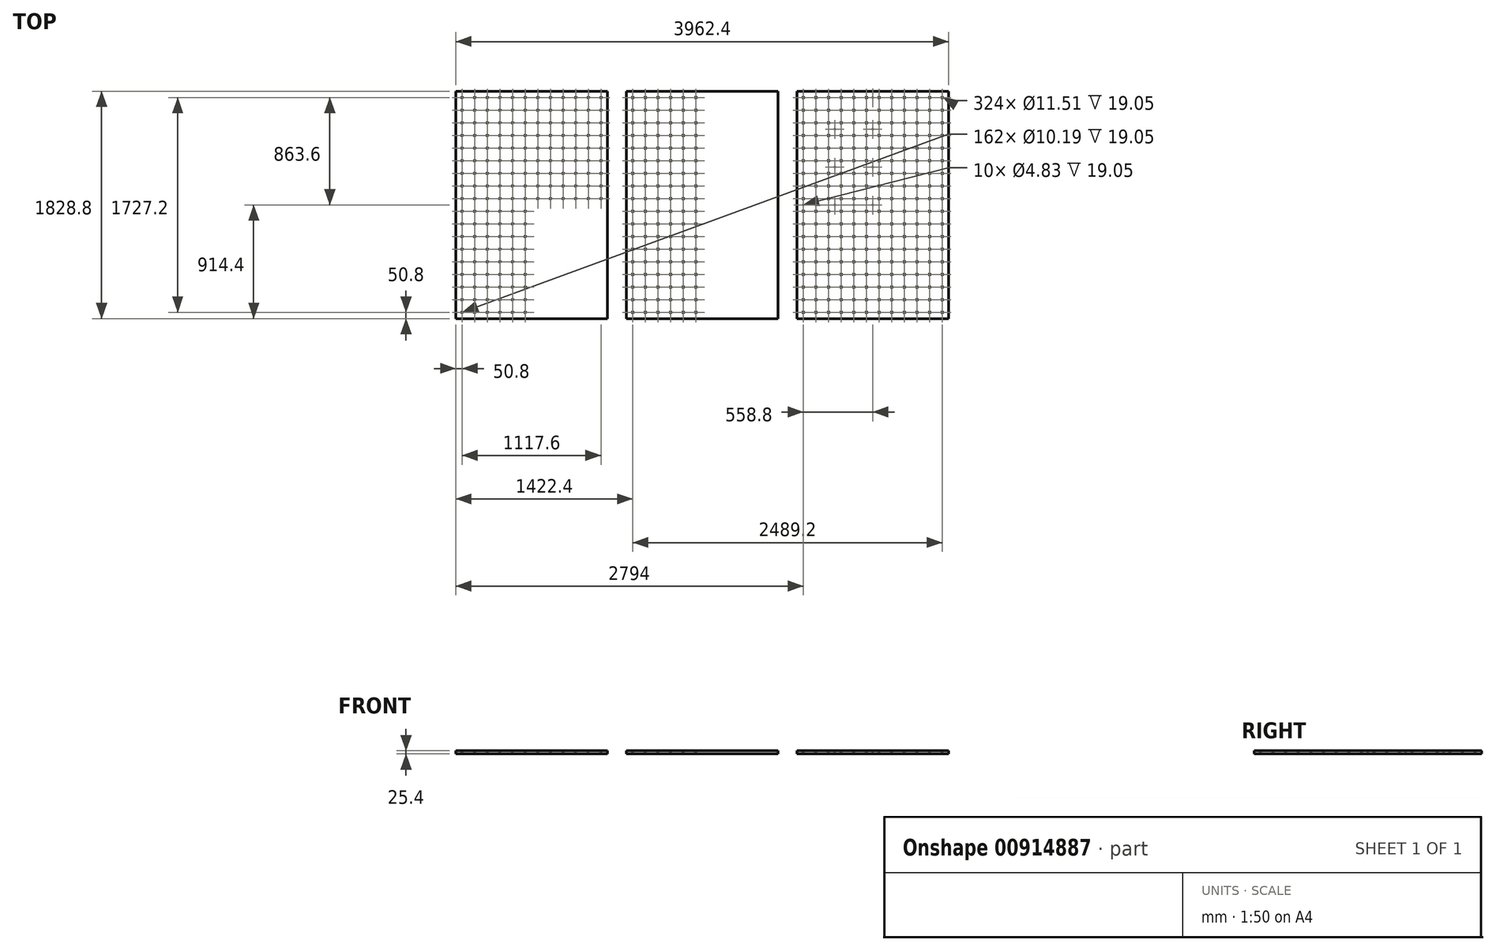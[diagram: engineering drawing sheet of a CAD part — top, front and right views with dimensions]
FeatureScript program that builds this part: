
annotation { "Feature Type Name" : "Feature", "Feature Type Description" : "" }
export const myFeature = defineFeature(function(context is Context, id is Id, definition is map)
    precondition{}
    {
        {
            var Q0;
            Q0=qCreatedBy(makeId("Top.planeOp"),FACE);
            var sketch = newSketch(context, id + "F0", { "sketchPlane" : qUnion([Q0])});
            skLineSegment(sketch, "E0.bottom", {"start": v(0, 1828.8) * mm, "end": v(1219.2, 1828.8) * mm});
            skLineSegment(sketch, "E0.top", {"start": v(0, 0) * mm, "end": v(1219.2, 0) * mm});
            skLineSegment(sketch, "E0.left", {"start": v(0, 1828.8) * mm, "end": v(0, 0) * mm});
            skLineSegment(sketch, "E0.right", {"start": v(1219.2, 1828.8) * mm, "end": v(1219.2, 0) * mm});
            skLineSegment(sketch, "E1", {"start": v(609.6, 1219.2) * mm, "end": v(609.6, 609.6) * mm, "construction": true});
            skLineSegment(sketch, "E2", {"start": v(304.8, 914.4) * mm, "end": v(914.4, 914.4) * mm, "construction": true});
            skSolve(sketch);
        }
        {
            var Q0;
            Q0=makeQuery(id+"F0.imprint","IMPRINT",FACE,{"disambiguationData":[TD([[makeQuery(id+"F0.imprint","IMPRINT",EDGE,{"derivedFrom":sQuery(id+"F0.wireOp",EDGE,"E0.bottom")}),-1.0]])]});
            extrude(context, id + "F1", {"entities" : qUnion([Q0]), "depth" : 25.4 * mm, "offsetDistance" : 25.4 * mm});
        }
        {
            var Q0;
            Q0=makeQuery(id+"F1.opExtrude","CAP_FACE",FACE,{"disambiguationData":[OSD([sQuery(id+"F0.wireOp",EDGE,"E0.bottom"),sQuery(id+"F0.wireOp",EDGE,"E0.top"),sQuery(id+"F0.wireOp",EDGE,"E0.left"),sQuery(id+"F0.wireOp",EDGE,"E0.right")])],"isStart":false});
            var sketch = newSketch(context, id + "F2", { "sketchPlane" : qUnion([Q0])});
            skCircle(sketch, "E3", {"center": v(558.8, 965.2) * mm, "radius": 5.75 * mm});
            skCircle(sketch, "E4.0.1.0", {"center": v(558.8, 1066.8) * mm, "radius": 5.75 * mm});
            skCircle(sketch, "E4.0.2.0", {"center": v(558.8, 1168.4) * mm, "radius": 5.75 * mm});
            skCircle(sketch, "E4.0.3.0", {"center": v(558.8, 1270) * mm, "radius": 5.75 * mm});
            skCircle(sketch, "E4.0.4.0", {"center": v(558.8, 1371.6) * mm, "radius": 5.75 * mm});
            skCircle(sketch, "E4.0.5.0", {"center": v(558.8, 1473.2) * mm, "radius": 5.75 * mm});
            skCircle(sketch, "E4.0.6.0", {"center": v(558.8, 1574.8) * mm, "radius": 5.75 * mm});
            skCircle(sketch, "E4.0.7.0", {"center": v(558.8, 1676.4) * mm, "radius": 5.75 * mm});
            skCircle(sketch, "E4.0.8.0", {"center": v(558.8, 1778) * mm, "radius": 5.75 * mm});
            skCircle(sketch, "E4.1.0.0", {"center": v(457.2, 965.2) * mm, "radius": 5.75 * mm});
            skCircle(sketch, "E4.1.1.0", {"center": v(457.2, 1066.8) * mm, "radius": 5.75 * mm});
            skCircle(sketch, "E4.1.2.0", {"center": v(457.2, 1168.4) * mm, "radius": 5.75 * mm});
            skCircle(sketch, "E4.1.3.0", {"center": v(457.2, 1270) * mm, "radius": 5.75 * mm});
            skCircle(sketch, "E4.1.4.0", {"center": v(457.2, 1371.6) * mm, "radius": 5.75 * mm});
            skCircle(sketch, "E4.1.5.0", {"center": v(457.2, 1473.2) * mm, "radius": 5.75 * mm});
            skCircle(sketch, "E4.1.6.0", {"center": v(457.2, 1574.8) * mm, "radius": 5.75 * mm});
            skCircle(sketch, "E4.1.7.0", {"center": v(457.2, 1676.4) * mm, "radius": 5.75 * mm});
            skCircle(sketch, "E4.1.8.0", {"center": v(457.2, 1778) * mm, "radius": 5.75 * mm});
            skCircle(sketch, "E4.2.0.0", {"center": v(355.6, 965.2) * mm, "radius": 5.75 * mm});
            skCircle(sketch, "E4.2.1.0", {"center": v(355.6, 1066.8) * mm, "radius": 5.75 * mm});
            skCircle(sketch, "E4.2.2.0", {"center": v(355.6, 1168.4) * mm, "radius": 5.75 * mm});
            skCircle(sketch, "E4.2.3.0", {"center": v(355.6, 1270) * mm, "radius": 5.75 * mm});
            skCircle(sketch, "E4.2.4.0", {"center": v(355.6, 1371.6) * mm, "radius": 5.75 * mm});
            skCircle(sketch, "E4.2.5.0", {"center": v(355.6, 1473.2) * mm, "radius": 5.75 * mm});
            skCircle(sketch, "E4.2.6.0", {"center": v(355.6, 1574.8) * mm, "radius": 5.75 * mm});
            skCircle(sketch, "E4.2.7.0", {"center": v(355.6, 1676.4) * mm, "radius": 5.75 * mm});
            skCircle(sketch, "E4.2.8.0", {"center": v(355.6, 1778) * mm, "radius": 5.75 * mm});
            skCircle(sketch, "E4.3.0.0", {"center": v(254, 965.2) * mm, "radius": 5.75 * mm});
            skCircle(sketch, "E4.3.1.0", {"center": v(254, 1066.8) * mm, "radius": 5.75 * mm});
            skCircle(sketch, "E4.3.2.0", {"center": v(254, 1168.4) * mm, "radius": 5.75 * mm});
            skCircle(sketch, "E4.3.3.0", {"center": v(254, 1270) * mm, "radius": 5.75 * mm});
            skCircle(sketch, "E4.3.4.0", {"center": v(254, 1371.6) * mm, "radius": 5.75 * mm});
            skCircle(sketch, "E4.3.5.0", {"center": v(254, 1473.2) * mm, "radius": 5.75 * mm});
            skCircle(sketch, "E4.3.6.0", {"center": v(254, 1574.8) * mm, "radius": 5.75 * mm});
            skCircle(sketch, "E4.3.7.0", {"center": v(254, 1676.4) * mm, "radius": 5.75 * mm});
            skCircle(sketch, "E4.3.8.0", {"center": v(254, 1778) * mm, "radius": 5.75 * mm});
            skCircle(sketch, "E4.4.0.0", {"center": v(152.4, 965.2) * mm, "radius": 5.75 * mm});
            skCircle(sketch, "E4.4.1.0", {"center": v(152.4, 1066.8) * mm, "radius": 5.75 * mm});
            skCircle(sketch, "E4.4.2.0", {"center": v(152.4, 1168.4) * mm, "radius": 5.75 * mm});
            skCircle(sketch, "E4.4.3.0", {"center": v(152.4, 1270) * mm, "radius": 5.75 * mm});
            skCircle(sketch, "E4.4.4.0", {"center": v(152.4, 1371.6) * mm, "radius": 5.75 * mm});
            skCircle(sketch, "E4.4.5.0", {"center": v(152.4, 1473.2) * mm, "radius": 5.75 * mm});
            skCircle(sketch, "E4.4.6.0", {"center": v(152.4, 1574.8) * mm, "radius": 5.75 * mm});
            skCircle(sketch, "E4.4.7.0", {"center": v(152.4, 1676.4) * mm, "radius": 5.75 * mm});
            skCircle(sketch, "E4.4.8.0", {"center": v(152.4, 1778) * mm, "radius": 5.75 * mm});
            skCircle(sketch, "E4.5.0.0", {"center": v(50.8, 965.2) * mm, "radius": 5.75 * mm});
            skCircle(sketch, "E4.5.1.0", {"center": v(50.8, 1066.8) * mm, "radius": 5.75 * mm});
            skCircle(sketch, "E4.5.2.0", {"center": v(50.8, 1168.4) * mm, "radius": 5.75 * mm});
            skCircle(sketch, "E4.5.3.0", {"center": v(50.8, 1270) * mm, "radius": 5.75 * mm});
            skCircle(sketch, "E4.5.4.0", {"center": v(50.8, 1371.6) * mm, "radius": 5.75 * mm});
            skCircle(sketch, "E4.5.5.0", {"center": v(50.8, 1473.2) * mm, "radius": 5.75 * mm});
            skCircle(sketch, "E4.5.6.0", {"center": v(50.8, 1574.8) * mm, "radius": 5.75 * mm});
            skCircle(sketch, "E4.5.7.0", {"center": v(50.8, 1676.4) * mm, "radius": 5.75 * mm});
            skCircle(sketch, "E4.5.8.0", {"center": v(50.8, 1778) * mm, "radius": 5.75 * mm});
            skLineSegment(sketch, "E4.direction1", {"start": v(558.8, 965.2) * mm, "end": v(457.2, 965.2) * mm, "construction": true});
            skLineSegment(sketch, "E4.direction2", {"start": v(558.8, 965.2) * mm, "end": v(558.8, 1066.8) * mm, "construction": true});
            skCircle(sketch, "E5.MirrorC", {"center": v(558.8, 863.6) * mm, "radius": 5.75 * mm});
            skCircle(sketch, "E6.MirrorC", {"center": v(558.8, 762) * mm, "radius": 5.75 * mm});
            skCircle(sketch, "E7.MirrorC", {"center": v(457.2, 863.6) * mm, "radius": 5.75 * mm});
            skCircle(sketch, "E8.MirrorC", {"center": v(254, 558.8) * mm, "radius": 5.75 * mm});
            skCircle(sketch, "E9.MirrorC", {"center": v(50.8, 558.8) * mm, "radius": 5.75 * mm});
            skCircle(sketch, "E10.MirrorC", {"center": v(355.6, 863.6) * mm, "radius": 5.75 * mm});
            skCircle(sketch, "E11.MirrorC", {"center": v(254, 863.6) * mm, "radius": 5.75 * mm});
            skCircle(sketch, "E12.MirrorC", {"center": v(355.6, 660.4) * mm, "radius": 5.75 * mm});
            skCircle(sketch, "E13.MirrorC", {"center": v(50.8, 762) * mm, "radius": 5.75 * mm});
            skCircle(sketch, "E14.MirrorC", {"center": v(355.6, 558.8) * mm, "radius": 5.75 * mm});
            skCircle(sketch, "E15.MirrorC", {"center": v(355.6, 762) * mm, "radius": 5.75 * mm});
            skCircle(sketch, "E16.MirrorC", {"center": v(254, 660.4) * mm, "radius": 5.75 * mm});
            skCircle(sketch, "E17.MirrorC", {"center": v(50.8, 863.6) * mm, "radius": 5.75 * mm});
            skCircle(sketch, "E18.MirrorC", {"center": v(152.4, 863.6) * mm, "radius": 5.75 * mm});
            skCircle(sketch, "E19.MirrorC", {"center": v(457.2, 558.8) * mm, "radius": 5.75 * mm});
            skCircle(sketch, "E20.MirrorC", {"center": v(457.2, 660.4) * mm, "radius": 5.75 * mm});
            skCircle(sketch, "E21.MirrorC", {"center": v(457.2, 762) * mm, "radius": 5.75 * mm});
            skCircle(sketch, "E22.MirrorC", {"center": v(152.4, 660.4) * mm, "radius": 5.75 * mm});
            skCircle(sketch, "E23.MirrorC", {"center": v(558.8, 558.8) * mm, "radius": 5.75 * mm});
            skCircle(sketch, "E24.MirrorC", {"center": v(152.4, 762) * mm, "radius": 5.75 * mm});
            skCircle(sketch, "E25.MirrorC", {"center": v(558.8, 660.4) * mm, "radius": 5.75 * mm});
            skCircle(sketch, "E26.MirrorC", {"center": v(254, 762) * mm, "radius": 5.75 * mm});
            skCircle(sketch, "E27.MirrorC", {"center": v(152.4, 558.8) * mm, "radius": 5.75 * mm});
            skCircle(sketch, "E28.MirrorC", {"center": v(50.8, 660.4) * mm, "radius": 5.75 * mm});
            skLineSegment(sketch, "E29.MirrorCS", {"start": v(558.8, 863.6) * mm, "end": v(457.2, 863.6) * mm, "construction": true});
            skLineSegment(sketch, "E30.MirrorCS", {"start": v(558.8, 863.6) * mm, "end": v(558.8, 762) * mm, "construction": true});
            skCircle(sketch, "E31.MirrorC", {"center": v(50.8, 355.6) * mm, "radius": 5.75 * mm});
            skCircle(sketch, "E32.MirrorC", {"center": v(355.6, 457.2) * mm, "radius": 5.75 * mm});
            skCircle(sketch, "E33.MirrorC", {"center": v(457.2, 457.2) * mm, "radius": 5.75 * mm});
            skCircle(sketch, "E34.MirrorC", {"center": v(457.2, 355.6) * mm, "radius": 5.75 * mm});
            skCircle(sketch, "E35.MirrorC", {"center": v(152.4, 152.4) * mm, "radius": 5.75 * mm});
            skCircle(sketch, "E36.MirrorC", {"center": v(50.8, 254) * mm, "radius": 5.75 * mm});
            skCircle(sketch, "E37.MirrorC", {"center": v(558.8, 457.2) * mm, "radius": 5.75 * mm});
            skCircle(sketch, "E38.MirrorC", {"center": v(254, 152.4) * mm, "radius": 5.75 * mm});
            skCircle(sketch, "E39.MirrorC", {"center": v(558.8, 152.4) * mm, "radius": 5.75 * mm});
            skCircle(sketch, "E40.MirrorC", {"center": v(558.8, 355.6) * mm, "radius": 5.75 * mm});
            skCircle(sketch, "E41.MirrorC", {"center": v(50.8, 50.8) * mm, "radius": 5.75 * mm});
            skCircle(sketch, "E42.MirrorC", {"center": v(558.8, 254) * mm, "radius": 5.75 * mm});
            skCircle(sketch, "E43.MirrorC", {"center": v(355.6, 152.4) * mm, "radius": 5.75 * mm});
            skCircle(sketch, "E44.MirrorC", {"center": v(152.4, 457.2) * mm, "radius": 5.75 * mm});
            skCircle(sketch, "E45.MirrorC", {"center": v(355.6, 355.6) * mm, "radius": 5.75 * mm});
            skCircle(sketch, "E46.MirrorC", {"center": v(558.8, 50.8) * mm, "radius": 5.75 * mm});
            skCircle(sketch, "E47.MirrorC", {"center": v(457.2, 50.8) * mm, "radius": 5.75 * mm});
            skCircle(sketch, "E48.MirrorC", {"center": v(254, 355.6) * mm, "radius": 5.75 * mm});
            skCircle(sketch, "E49.MirrorC", {"center": v(254, 254) * mm, "radius": 5.75 * mm});
            skCircle(sketch, "E50.MirrorC", {"center": v(457.2, 152.4) * mm, "radius": 5.75 * mm});
            skCircle(sketch, "E51.MirrorC", {"center": v(50.8, 152.4) * mm, "radius": 5.75 * mm});
            skCircle(sketch, "E52.MirrorC", {"center": v(355.6, 50.8) * mm, "radius": 5.75 * mm});
            skCircle(sketch, "E53.MirrorC", {"center": v(152.4, 355.6) * mm, "radius": 5.75 * mm});
            skCircle(sketch, "E54.MirrorC", {"center": v(457.2, 254) * mm, "radius": 5.75 * mm});
            skCircle(sketch, "E55.MirrorC", {"center": v(355.6, 254) * mm, "radius": 5.75 * mm});
            skCircle(sketch, "E56.MirrorC", {"center": v(152.4, 50.8) * mm, "radius": 5.75 * mm});
            skCircle(sketch, "E57.MirrorC", {"center": v(50.8, 457.2) * mm, "radius": 5.75 * mm});
            skCircle(sketch, "E58.MirrorC", {"center": v(254, 50.8) * mm, "radius": 5.75 * mm});
            skCircle(sketch, "E59.MirrorC", {"center": v(254, 457.2) * mm, "radius": 5.75 * mm});
            skCircle(sketch, "E60.MirrorC", {"center": v(152.4, 254) * mm, "radius": 5.75 * mm});
            skSolve(sketch);
        }
        {
            var Q0;
            Q0 = qSketchRegion(id + "F2", true);
            extrude(context, id + "F3", {"entities" : qUnion([Q0]), "operationType" : NewBodyOperationType.REMOVE, "oppositeDirection" : true, "depth" : 19.05 * mm, "offsetDistance" : 25.4 * mm});
        }
        {
            var Q0;
            Q0=qCreatedBy(makeId("Top.planeOp"),FACE);
            var sketch = newSketch(context, id + "F4", { "sketchPlane" : qUnion([Q0])});
            skLineSegment(sketch, "E61.bottom", {"start": v(-1371.6, 1828.8) * mm, "end": v(-152.4, 1828.8) * mm});
            skLineSegment(sketch, "E61.top", {"start": v(-1371.6, 0) * mm, "end": v(-152.4, 0) * mm});
            skLineSegment(sketch, "E61.left", {"start": v(-1371.6, 1828.8) * mm, "end": v(-1371.6, 0) * mm});
            skLineSegment(sketch, "E61.right", {"start": v(-152.4, 1828.8) * mm, "end": v(-152.4, 0) * mm});
            skLineSegment(sketch, "E62", {"start": v(-762, 1219.2) * mm, "end": v(-762, 609.6) * mm, "construction": true});
            skLineSegment(sketch, "E63", {"start": v(-1066.8, 914.4) * mm, "end": v(-457.2, 914.4) * mm, "construction": true});
            skSolve(sketch);
        }
        {
            var Q0;
            Q0=makeQuery(id+"F4.imprint","IMPRINT",FACE,{"disambiguationData":[TD([[makeQuery(id+"F4.imprint","IMPRINT",EDGE,{"derivedFrom":sQuery(id+"F4.wireOp",EDGE,"E61.bottom")}),-1.0]])]});
            extrude(context, id + "F5", {"entities" : qUnion([Q0]), "depth" : 25.4 * mm, "offsetDistance" : 25.4 * mm});
        }
        {
            var Q0;
            Q0=makeQuery(id+"F5.opExtrude","CAP_FACE",FACE,{"disambiguationData":[OSD([sQuery(id+"F4.wireOp",EDGE,"E61.bottom"),sQuery(id+"F4.wireOp",EDGE,"E61.top"),sQuery(id+"F4.wireOp",EDGE,"E61.left"),sQuery(id+"F4.wireOp",EDGE,"E61.right")])],"isStart":false});
            var sketch = newSketch(context, id + "F6", { "sketchPlane" : qUnion([Q0])});
            skCircle(sketch, "E64", {"center": v(-812.8, 965.2) * mm, "radius": 5.1 * mm});
            skCircle(sketch, "E65.0.1.0", {"center": v(-812.8, 1066.8) * mm, "radius": 5.1 * mm});
            skCircle(sketch, "E65.0.2.0", {"center": v(-812.8, 1168.4) * mm, "radius": 5.1 * mm});
            skCircle(sketch, "E65.0.3.0", {"center": v(-812.8, 1270) * mm, "radius": 5.1 * mm});
            skCircle(sketch, "E65.0.4.0", {"center": v(-812.8, 1371.6) * mm, "radius": 5.1 * mm});
            skCircle(sketch, "E65.0.5.0", {"center": v(-812.8, 1473.2) * mm, "radius": 5.1 * mm});
            skCircle(sketch, "E65.0.6.0", {"center": v(-812.8, 1574.8) * mm, "radius": 5.1 * mm});
            skCircle(sketch, "E65.0.7.0", {"center": v(-812.8, 1676.4) * mm, "radius": 5.1 * mm});
            skCircle(sketch, "E65.0.8.0", {"center": v(-812.8, 1778) * mm, "radius": 5.1 * mm});
            skCircle(sketch, "E65.1.0.0", {"center": v(-914.4, 965.2) * mm, "radius": 5.1 * mm});
            skCircle(sketch, "E65.1.1.0", {"center": v(-914.4, 1066.8) * mm, "radius": 5.1 * mm});
            skCircle(sketch, "E65.1.2.0", {"center": v(-914.4, 1168.4) * mm, "radius": 5.1 * mm});
            skCircle(sketch, "E65.1.3.0", {"center": v(-914.4, 1270) * mm, "radius": 5.1 * mm});
            skCircle(sketch, "E65.1.4.0", {"center": v(-914.4, 1371.6) * mm, "radius": 5.1 * mm});
            skCircle(sketch, "E65.1.5.0", {"center": v(-914.4, 1473.2) * mm, "radius": 5.1 * mm});
            skCircle(sketch, "E65.1.6.0", {"center": v(-914.4, 1574.8) * mm, "radius": 5.1 * mm});
            skCircle(sketch, "E65.1.7.0", {"center": v(-914.4, 1676.4) * mm, "radius": 5.1 * mm});
            skCircle(sketch, "E65.1.8.0", {"center": v(-914.4, 1778) * mm, "radius": 5.1 * mm});
            skCircle(sketch, "E65.2.0.0", {"center": v(-1016, 965.2) * mm, "radius": 5.1 * mm});
            skCircle(sketch, "E65.2.1.0", {"center": v(-1016, 1066.8) * mm, "radius": 5.1 * mm});
            skCircle(sketch, "E65.2.2.0", {"center": v(-1016, 1168.4) * mm, "radius": 5.1 * mm});
            skCircle(sketch, "E65.2.3.0", {"center": v(-1016, 1270) * mm, "radius": 5.1 * mm});
            skCircle(sketch, "E65.2.4.0", {"center": v(-1016, 1371.6) * mm, "radius": 5.1 * mm});
            skCircle(sketch, "E65.2.5.0", {"center": v(-1016, 1473.2) * mm, "radius": 5.1 * mm});
            skCircle(sketch, "E65.2.6.0", {"center": v(-1016, 1574.8) * mm, "radius": 5.1 * mm});
            skCircle(sketch, "E65.2.7.0", {"center": v(-1016, 1676.4) * mm, "radius": 5.1 * mm});
            skCircle(sketch, "E65.2.8.0", {"center": v(-1016, 1778) * mm, "radius": 5.1 * mm});
            skCircle(sketch, "E65.3.0.0", {"center": v(-1117.6, 965.2) * mm, "radius": 5.1 * mm});
            skCircle(sketch, "E65.3.1.0", {"center": v(-1117.6, 1066.8) * mm, "radius": 5.1 * mm});
            skCircle(sketch, "E65.3.2.0", {"center": v(-1117.6, 1168.4) * mm, "radius": 5.1 * mm});
            skCircle(sketch, "E65.3.3.0", {"center": v(-1117.6, 1270) * mm, "radius": 5.1 * mm});
            skCircle(sketch, "E65.3.4.0", {"center": v(-1117.6, 1371.6) * mm, "radius": 5.1 * mm});
            skCircle(sketch, "E65.3.5.0", {"center": v(-1117.6, 1473.2) * mm, "radius": 5.1 * mm});
            skCircle(sketch, "E65.3.6.0", {"center": v(-1117.6, 1574.8) * mm, "radius": 5.1 * mm});
            skCircle(sketch, "E65.3.7.0", {"center": v(-1117.6, 1676.4) * mm, "radius": 5.1 * mm});
            skCircle(sketch, "E65.3.8.0", {"center": v(-1117.6, 1778) * mm, "radius": 5.1 * mm});
            skCircle(sketch, "E65.4.0.0", {"center": v(-1219.2, 965.2) * mm, "radius": 5.1 * mm});
            skCircle(sketch, "E65.4.1.0", {"center": v(-1219.2, 1066.8) * mm, "radius": 5.1 * mm});
            skCircle(sketch, "E65.4.2.0", {"center": v(-1219.2, 1168.4) * mm, "radius": 5.1 * mm});
            skCircle(sketch, "E65.4.3.0", {"center": v(-1219.2, 1270) * mm, "radius": 5.1 * mm});
            skCircle(sketch, "E65.4.4.0", {"center": v(-1219.2, 1371.6) * mm, "radius": 5.1 * mm});
            skCircle(sketch, "E65.4.5.0", {"center": v(-1219.2, 1473.2) * mm, "radius": 5.1 * mm});
            skCircle(sketch, "E65.4.6.0", {"center": v(-1219.2, 1574.8) * mm, "radius": 5.1 * mm});
            skCircle(sketch, "E65.4.7.0", {"center": v(-1219.2, 1676.4) * mm, "radius": 5.1 * mm});
            skCircle(sketch, "E65.4.8.0", {"center": v(-1219.2, 1778) * mm, "radius": 5.1 * mm});
            skCircle(sketch, "E65.5.0.0", {"center": v(-1320.8, 965.2) * mm, "radius": 5.1 * mm});
            skCircle(sketch, "E65.5.1.0", {"center": v(-1320.8, 1066.8) * mm, "radius": 5.1 * mm});
            skCircle(sketch, "E65.5.2.0", {"center": v(-1320.8, 1168.4) * mm, "radius": 5.1 * mm});
            skCircle(sketch, "E65.5.3.0", {"center": v(-1320.8, 1270) * mm, "radius": 5.1 * mm});
            skCircle(sketch, "E65.5.4.0", {"center": v(-1320.8, 1371.6) * mm, "radius": 5.1 * mm});
            skCircle(sketch, "E65.5.5.0", {"center": v(-1320.8, 1473.2) * mm, "radius": 5.1 * mm});
            skCircle(sketch, "E65.5.6.0", {"center": v(-1320.8, 1574.8) * mm, "radius": 5.1 * mm});
            skCircle(sketch, "E65.5.7.0", {"center": v(-1320.8, 1676.4) * mm, "radius": 5.1 * mm});
            skCircle(sketch, "E65.5.8.0", {"center": v(-1320.8, 1778) * mm, "radius": 5.1 * mm});
            skLineSegment(sketch, "E65.direction1", {"start": v(-812.8, 965.2) * mm, "end": v(-914.4, 965.2) * mm, "construction": true});
            skLineSegment(sketch, "E65.direction2", {"start": v(-812.8, 965.2) * mm, "end": v(-812.8, 1066.8) * mm, "construction": true});
            skCircle(sketch, "E66.MirrorC", {"center": v(-812.8, 863.6) * mm, "radius": 5.1 * mm});
            skCircle(sketch, "E67.MirrorC", {"center": v(-812.8, 762) * mm, "radius": 5.1 * mm});
            skCircle(sketch, "E68.MirrorC", {"center": v(-914.4, 863.6) * mm, "radius": 5.1 * mm});
            skCircle(sketch, "E69.MirrorC", {"center": v(-1219.2, 254) * mm, "radius": 5.1 * mm});
            skCircle(sketch, "E70.MirrorC", {"center": v(-1016, 254) * mm, "radius": 5.1 * mm});
            skCircle(sketch, "E71.MirrorC", {"center": v(-1219.2, 152.4) * mm, "radius": 5.1 * mm});
            skCircle(sketch, "E72.MirrorC", {"center": v(-812.8, 355.6) * mm, "radius": 5.1 * mm});
            skCircle(sketch, "E73.MirrorC", {"center": v(-1016, 660.4) * mm, "radius": 5.1 * mm});
            skCircle(sketch, "E74.MirrorC", {"center": v(-812.8, 558.8) * mm, "radius": 5.1 * mm});
            skCircle(sketch, "E75.MirrorC", {"center": v(-1219.2, 660.4) * mm, "radius": 5.1 * mm});
            skCircle(sketch, "E76.MirrorC", {"center": v(-1219.2, 355.6) * mm, "radius": 5.1 * mm});
            skCircle(sketch, "E77.MirrorC", {"center": v(-812.8, 254) * mm, "radius": 5.1 * mm});
            skCircle(sketch, "E78.MirrorC", {"center": v(-1320.8, 152.4) * mm, "radius": 5.1 * mm});
            skCircle(sketch, "E79.MirrorC", {"center": v(-1117.6, 355.6) * mm, "radius": 5.1 * mm});
            skCircle(sketch, "E80.MirrorC", {"center": v(-1117.6, 660.4) * mm, "radius": 5.1 * mm});
            skCircle(sketch, "E81.MirrorC", {"center": v(-914.4, 457.2) * mm, "radius": 5.1 * mm});
            skCircle(sketch, "E82.MirrorC", {"center": v(-914.4, 660.4) * mm, "radius": 5.1 * mm});
            skCircle(sketch, "E83.MirrorC", {"center": v(-1117.6, 254) * mm, "radius": 5.1 * mm});
            skCircle(sketch, "E84.MirrorC", {"center": v(-812.8, 152.4) * mm, "radius": 5.1 * mm});
            skCircle(sketch, "E85.MirrorC", {"center": v(-1016, 355.6) * mm, "radius": 5.1 * mm});
            skCircle(sketch, "E86.MirrorC", {"center": v(-1117.6, 558.8) * mm, "radius": 5.1 * mm});
            skCircle(sketch, "E87.MirrorC", {"center": v(-914.4, 254) * mm, "radius": 5.1 * mm});
            skCircle(sketch, "E88.MirrorC", {"center": v(-812.8, 457.2) * mm, "radius": 5.1 * mm});
            skCircle(sketch, "E89.MirrorC", {"center": v(-914.4, 355.6) * mm, "radius": 5.1 * mm});
            skCircle(sketch, "E90.MirrorC", {"center": v(-1320.8, 355.6) * mm, "radius": 5.1 * mm});
            skCircle(sketch, "E91.MirrorC", {"center": v(-812.8, 660.4) * mm, "radius": 5.1 * mm});
            skCircle(sketch, "E92.MirrorC", {"center": v(-914.4, 152.4) * mm, "radius": 5.1 * mm});
            skCircle(sketch, "E93.MirrorC", {"center": v(-812.8, 50.8) * mm, "radius": 5.1 * mm});
            skCircle(sketch, "E94.MirrorC", {"center": v(-1219.2, 558.8) * mm, "radius": 5.1 * mm});
            skCircle(sketch, "E95.MirrorC", {"center": v(-1320.8, 762) * mm, "radius": 5.1 * mm});
            skCircle(sketch, "E96.MirrorC", {"center": v(-1016, 457.2) * mm, "radius": 5.1 * mm});
            skCircle(sketch, "E97.MirrorC", {"center": v(-1117.6, 152.4) * mm, "radius": 5.1 * mm});
            skCircle(sketch, "E98.MirrorC", {"center": v(-1016, 152.4) * mm, "radius": 5.1 * mm});
            skCircle(sketch, "E99.MirrorC", {"center": v(-1117.6, 863.6) * mm, "radius": 5.1 * mm});
            skCircle(sketch, "E100.MirrorC", {"center": v(-1320.8, 50.8) * mm, "radius": 5.1 * mm});
            skCircle(sketch, "E101.MirrorC", {"center": v(-1219.2, 863.6) * mm, "radius": 5.1 * mm});
            skCircle(sketch, "E102.MirrorC", {"center": v(-1016, 50.8) * mm, "radius": 5.1 * mm});
            skCircle(sketch, "E103.MirrorC", {"center": v(-1016, 558.8) * mm, "radius": 5.1 * mm});
            skCircle(sketch, "E104.MirrorC", {"center": v(-1320.8, 254) * mm, "radius": 5.1 * mm});
            skCircle(sketch, "E105.MirrorC", {"center": v(-1117.6, 762) * mm, "radius": 5.1 * mm});
            skCircle(sketch, "E106.MirrorC", {"center": v(-1117.6, 457.2) * mm, "radius": 5.1 * mm});
            skCircle(sketch, "E107.MirrorC", {"center": v(-1117.6, 50.8) * mm, "radius": 5.1 * mm});
            skCircle(sketch, "E108.MirrorC", {"center": v(-1320.8, 660.4) * mm, "radius": 5.1 * mm});
            skCircle(sketch, "E109.MirrorC", {"center": v(-1320.8, 863.6) * mm, "radius": 5.1 * mm});
            skCircle(sketch, "E110.MirrorC", {"center": v(-1320.8, 558.8) * mm, "radius": 5.1 * mm});
            skCircle(sketch, "E111.MirrorC", {"center": v(-914.4, 762) * mm, "radius": 5.1 * mm});
            skCircle(sketch, "E112.MirrorC", {"center": v(-1320.8, 457.2) * mm, "radius": 5.1 * mm});
            skCircle(sketch, "E113.MirrorC", {"center": v(-914.4, 50.8) * mm, "radius": 5.1 * mm});
            skCircle(sketch, "E114.MirrorC", {"center": v(-1219.2, 50.8) * mm, "radius": 5.1 * mm});
            skCircle(sketch, "E115.MirrorC", {"center": v(-1219.2, 762) * mm, "radius": 5.1 * mm});
            skCircle(sketch, "E116.MirrorC", {"center": v(-1016, 762) * mm, "radius": 5.1 * mm});
            skCircle(sketch, "E117.MirrorC", {"center": v(-1219.2, 457.2) * mm, "radius": 5.1 * mm});
            skCircle(sketch, "E118.MirrorC", {"center": v(-1016, 863.6) * mm, "radius": 5.1 * mm});
            skCircle(sketch, "E119.MirrorC", {"center": v(-914.4, 558.8) * mm, "radius": 5.1 * mm});
            skLineSegment(sketch, "E120.MirrorCS", {"start": v(-812.8, 863.6) * mm, "end": v(-914.4, 863.6) * mm, "construction": true});
            skLineSegment(sketch, "E121.MirrorCS", {"start": v(-812.8, 863.6) * mm, "end": v(-812.8, 762) * mm, "construction": true});
            skCircle(sketch, "E122.MirrorC", {"center": v(-711.2, 965.2) * mm, "radius": 5.1 * mm});
            skCircle(sketch, "E123.MirrorC", {"center": v(-609.6, 965.2) * mm, "radius": 5.1 * mm});
            skCircle(sketch, "E124.MirrorC", {"center": v(-711.2, 1066.8) * mm, "radius": 5.1 * mm});
            skCircle(sketch, "E125.MirrorC", {"center": v(-203.2, 1778) * mm, "radius": 5.1 * mm});
            skCircle(sketch, "E126.MirrorC", {"center": v(-304.8, 1066.8) * mm, "radius": 5.1 * mm});
            skCircle(sketch, "E127.MirrorC", {"center": v(-304.8, 1371.6) * mm, "radius": 5.1 * mm});
            skCircle(sketch, "E128.MirrorC", {"center": v(-508, 1676.4) * mm, "radius": 5.1 * mm});
            skCircle(sketch, "E129.MirrorC", {"center": v(-304.8, 1473.2) * mm, "radius": 5.1 * mm});
            skCircle(sketch, "E130.MirrorC", {"center": v(-508, 1066.8) * mm, "radius": 5.1 * mm});
            skCircle(sketch, "E131.MirrorC", {"center": v(-406.4, 1371.6) * mm, "radius": 5.1 * mm});
            skCircle(sketch, "E132.MirrorC", {"center": v(-711.2, 1676.4) * mm, "radius": 5.1 * mm});
            skCircle(sketch, "E133.MirrorC", {"center": v(-609.6, 1473.2) * mm, "radius": 5.1 * mm});
            skCircle(sketch, "E134.MirrorC", {"center": v(-711.2, 1371.6) * mm, "radius": 5.1 * mm});
            skCircle(sketch, "E135.MirrorC", {"center": v(-304.8, 1574.8) * mm, "radius": 5.1 * mm});
            skCircle(sketch, "E136.MirrorC", {"center": v(-406.4, 1473.2) * mm, "radius": 5.1 * mm});
            skCircle(sketch, "E137.MirrorC", {"center": v(-203.2, 1676.4) * mm, "radius": 5.1 * mm});
            skCircle(sketch, "E138.MirrorC", {"center": v(-203.2, 1371.6) * mm, "radius": 5.1 * mm});
            skCircle(sketch, "E139.MirrorC", {"center": v(-203.2, 1574.8) * mm, "radius": 5.1 * mm});
            skCircle(sketch, "E140.MirrorC", {"center": v(-609.6, 1270) * mm, "radius": 5.1 * mm});
            skCircle(sketch, "E141.MirrorC", {"center": v(-203.2, 1270) * mm, "radius": 5.1 * mm});
            skCircle(sketch, "E142.MirrorC", {"center": v(-508, 1371.6) * mm, "radius": 5.1 * mm});
            skCircle(sketch, "E143.MirrorC", {"center": v(-304.8, 965.2) * mm, "radius": 5.1 * mm});
            skCircle(sketch, "E144.MirrorC", {"center": v(-304.8, 1168.4) * mm, "radius": 5.1 * mm});
            skCircle(sketch, "E145.MirrorC", {"center": v(-203.2, 1066.8) * mm, "radius": 5.1 * mm});
            skCircle(sketch, "E146.MirrorC", {"center": v(-406.4, 1574.8) * mm, "radius": 5.1 * mm});
            skCircle(sketch, "E147.MirrorC", {"center": v(-508, 1270) * mm, "radius": 5.1 * mm});
            skCircle(sketch, "E148.MirrorC", {"center": v(-609.6, 1168.4) * mm, "radius": 5.1 * mm});
            skCircle(sketch, "E149.MirrorC", {"center": v(-406.4, 965.2) * mm, "radius": 5.1 * mm});
            skCircle(sketch, "E150.MirrorC", {"center": v(-609.6, 1574.8) * mm, "radius": 5.1 * mm});
            skCircle(sketch, "E151.MirrorC", {"center": v(-711.2, 1778) * mm, "radius": 5.1 * mm});
            skCircle(sketch, "E152.MirrorC", {"center": v(-406.4, 1066.8) * mm, "radius": 5.1 * mm});
            skCircle(sketch, "E153.MirrorC", {"center": v(-609.6, 1066.8) * mm, "radius": 5.1 * mm});
            skCircle(sketch, "E154.MirrorC", {"center": v(-406.4, 1778) * mm, "radius": 5.1 * mm});
            skCircle(sketch, "E155.MirrorC", {"center": v(-304.8, 1270) * mm, "radius": 5.1 * mm});
            skCircle(sketch, "E156.MirrorC", {"center": v(-508, 1574.8) * mm, "radius": 5.1 * mm});
            skCircle(sketch, "E157.MirrorC", {"center": v(-711.2, 1473.2) * mm, "radius": 5.1 * mm});
            skCircle(sketch, "E158.MirrorC", {"center": v(-406.4, 1270) * mm, "radius": 5.1 * mm});
            skCircle(sketch, "E159.MirrorC", {"center": v(-304.8, 1676.4) * mm, "radius": 5.1 * mm});
            skCircle(sketch, "E160.MirrorC", {"center": v(-711.2, 1168.4) * mm, "radius": 5.1 * mm});
            skCircle(sketch, "E161.MirrorC", {"center": v(-203.2, 965.2) * mm, "radius": 5.1 * mm});
            skCircle(sketch, "E162.MirrorC", {"center": v(-304.8, 1778) * mm, "radius": 5.1 * mm});
            skCircle(sketch, "E163.MirrorC", {"center": v(-711.2, 1574.8) * mm, "radius": 5.1 * mm});
            skCircle(sketch, "E164.MirrorC", {"center": v(-711.2, 1270) * mm, "radius": 5.1 * mm});
            skCircle(sketch, "E165.MirrorC", {"center": v(-609.6, 1371.6) * mm, "radius": 5.1 * mm});
            skCircle(sketch, "E166.MirrorC", {"center": v(-609.6, 1676.4) * mm, "radius": 5.1 * mm});
            skCircle(sketch, "E167.MirrorC", {"center": v(-203.2, 1473.2) * mm, "radius": 5.1 * mm});
            skCircle(sketch, "E168.MirrorC", {"center": v(-508, 1168.4) * mm, "radius": 5.1 * mm});
            skCircle(sketch, "E169.MirrorC", {"center": v(-508, 965.2) * mm, "radius": 5.1 * mm});
            skCircle(sketch, "E170.MirrorC", {"center": v(-406.4, 1676.4) * mm, "radius": 5.1 * mm});
            skCircle(sketch, "E171.MirrorC", {"center": v(-508, 1473.2) * mm, "radius": 5.1 * mm});
            skCircle(sketch, "E172.MirrorC", {"center": v(-406.4, 1168.4) * mm, "radius": 5.1 * mm});
            skCircle(sketch, "E173.MirrorC", {"center": v(-609.6, 1778) * mm, "radius": 5.1 * mm});
            skCircle(sketch, "E174.MirrorC", {"center": v(-508, 1778) * mm, "radius": 5.1 * mm});
            skCircle(sketch, "E175.MirrorC", {"center": v(-203.2, 1168.4) * mm, "radius": 5.1 * mm});
            skLineSegment(sketch, "E176.MirrorCS", {"start": v(-711.2, 965.2) * mm, "end": v(-711.2, 1066.8) * mm, "construction": true});
            skLineSegment(sketch, "E177.MirrorCS", {"start": v(-711.2, 965.2) * mm, "end": v(-609.6, 965.2) * mm, "construction": true});
            skSolve(sketch);
        }
        {
            var Q0;
            Q0 = qSketchRegion(id + "F6", true);
            extrude(context, id + "F7", {"entities" : qUnion([Q0]), "operationType" : NewBodyOperationType.REMOVE, "oppositeDirection" : true, "depth" : 19.05 * mm, "offsetDistance" : 25.4 * mm});
        }
        {
            var Q0;
            Q0=qCreatedBy(makeId("Top.planeOp"),FACE);
            var sketch = newSketch(context, id + "F8", { "sketchPlane" : qUnion([Q0])});
            skLineSegment(sketch, "E178.bottom", {"start": v(1371.6, 1828.8) * mm, "end": v(2590.8, 1828.8) * mm});
            skLineSegment(sketch, "E178.top", {"start": v(1371.6, 0) * mm, "end": v(2590.8, 0) * mm});
            skLineSegment(sketch, "E178.left", {"start": v(1371.6, 1828.8) * mm, "end": v(1371.6, 0) * mm});
            skLineSegment(sketch, "E178.right", {"start": v(2590.8, 1828.8) * mm, "end": v(2590.8, 0) * mm});
            skLineSegment(sketch, "E179", {"start": v(1981.2, 1219.2) * mm, "end": v(1981.2, 609.6) * mm, "construction": true});
            skLineSegment(sketch, "E180", {"start": v(1676.4, 914.4) * mm, "end": v(2286, 914.4) * mm, "construction": true});
            skSolve(sketch);
        }
        {
            var Q0;
            Q0 = qSketchRegion(id + "F8", true);
            extrude(context, id + "F9", {"entities" : qUnion([Q0]), "depth" : 25.4 * mm, "offsetDistance" : 25.4 * mm});
        }
        {
            var Q0;
            Q0=makeQuery(id+"F9.opExtrude","CAP_FACE",FACE,{"disambiguationData":[OSD([sQuery(id+"F8.wireOp",EDGE,"E178.bottom"),sQuery(id+"F8.wireOp",EDGE,"E178.top"),sQuery(id+"F8.wireOp",EDGE,"E178.left"),sQuery(id+"F8.wireOp",EDGE,"E178.right")])],"isStart":false});
            var sketch = newSketch(context, id + "F10", { "sketchPlane" : qUnion([Q0])});
            skCircle(sketch, "E181", {"center": v(1422.4, 1778) * mm, "radius": 5.75 * mm});
            skCircle(sketch, "E182.0.1.0", {"center": v(1422.4, 1676.4) * mm, "radius": 5.75 * mm});
            skCircle(sketch, "E182.0.2.0", {"center": v(1422.4, 1574.8) * mm, "radius": 5.75 * mm});
            skCircle(sketch, "E182.0.3.0", {"center": v(1422.4, 1473.2) * mm, "radius": 5.75 * mm});
            skCircle(sketch, "E182.0.4.0", {"center": v(1422.4, 1371.6) * mm, "radius": 5.75 * mm});
            skCircle(sketch, "E182.0.5.0", {"center": v(1422.4, 1270) * mm, "radius": 5.75 * mm});
            skCircle(sketch, "E182.0.6.0", {"center": v(1422.4, 1168.4) * mm, "radius": 5.75 * mm});
            skCircle(sketch, "E182.0.7.0", {"center": v(1422.4, 1066.8) * mm, "radius": 5.75 * mm});
            skCircle(sketch, "E182.0.8.0", {"center": v(1422.4, 965.2) * mm, "radius": 5.75 * mm});
            skCircle(sketch, "E182.0.9.0", {"center": v(1422.4, 863.6) * mm, "radius": 5.75 * mm});
            skCircle(sketch, "E182.0.10.0", {"center": v(1422.4, 762) * mm, "radius": 5.75 * mm});
            skCircle(sketch, "E182.0.11.0", {"center": v(1422.4, 660.4) * mm, "radius": 5.75 * mm});
            skCircle(sketch, "E182.0.12.0", {"center": v(1422.4, 558.8) * mm, "radius": 5.75 * mm});
            skCircle(sketch, "E182.0.13.0", {"center": v(1422.4, 457.2) * mm, "radius": 5.75 * mm});
            skCircle(sketch, "E182.0.14.0", {"center": v(1422.4, 355.6) * mm, "radius": 5.75 * mm});
            skCircle(sketch, "E182.0.15.0", {"center": v(1422.4, 254) * mm, "radius": 5.75 * mm});
            skCircle(sketch, "E182.0.16.0", {"center": v(1422.4, 152.4) * mm, "radius": 5.75 * mm});
            skCircle(sketch, "E182.0.17.0", {"center": v(1422.4, 50.8) * mm, "radius": 5.75 * mm});
            skCircle(sketch, "E182.1.0.0", {"center": v(1524, 1778) * mm, "radius": 5.75 * mm});
            skCircle(sketch, "E182.1.1.0", {"center": v(1524, 1676.4) * mm, "radius": 5.75 * mm});
            skCircle(sketch, "E182.1.2.0", {"center": v(1524, 1574.8) * mm, "radius": 5.75 * mm});
            skCircle(sketch, "E182.1.3.0", {"center": v(1524, 1473.2) * mm, "radius": 5.75 * mm});
            skCircle(sketch, "E182.1.4.0", {"center": v(1524, 1371.6) * mm, "radius": 5.75 * mm});
            skCircle(sketch, "E182.1.5.0", {"center": v(1524, 1270) * mm, "radius": 5.75 * mm});
            skCircle(sketch, "E182.1.6.0", {"center": v(1524, 1168.4) * mm, "radius": 5.75 * mm});
            skCircle(sketch, "E182.1.7.0", {"center": v(1524, 1066.8) * mm, "radius": 5.75 * mm});
            skCircle(sketch, "E182.1.8.0", {"center": v(1524, 965.2) * mm, "radius": 5.75 * mm});
            skCircle(sketch, "E182.1.9.0", {"center": v(1524, 863.6) * mm, "radius": 5.75 * mm});
            skCircle(sketch, "E182.1.10.0", {"center": v(1524, 762) * mm, "radius": 5.75 * mm});
            skCircle(sketch, "E182.1.11.0", {"center": v(1524, 660.4) * mm, "radius": 5.75 * mm});
            skCircle(sketch, "E182.1.12.0", {"center": v(1524, 558.8) * mm, "radius": 5.75 * mm});
            skCircle(sketch, "E182.1.13.0", {"center": v(1524, 457.2) * mm, "radius": 5.75 * mm});
            skCircle(sketch, "E182.1.14.0", {"center": v(1524, 355.6) * mm, "radius": 5.75 * mm});
            skCircle(sketch, "E182.1.15.0", {"center": v(1524, 254) * mm, "radius": 5.75 * mm});
            skCircle(sketch, "E182.1.16.0", {"center": v(1524, 152.4) * mm, "radius": 5.75 * mm});
            skCircle(sketch, "E182.1.17.0", {"center": v(1524, 50.8) * mm, "radius": 5.75 * mm});
            skCircle(sketch, "E182.2.0.0", {"center": v(1625.6, 1778) * mm, "radius": 5.75 * mm});
            skCircle(sketch, "E182.2.1.0", {"center": v(1625.6, 1676.4) * mm, "radius": 5.75 * mm});
            skCircle(sketch, "E182.2.2.0", {"center": v(1625.6, 1574.8) * mm, "radius": 5.75 * mm});
            skCircle(sketch, "E182.2.3.0", {"center": v(1625.6, 1473.2) * mm, "radius": 5.75 * mm});
            skCircle(sketch, "E182.2.4.0", {"center": v(1625.6, 1371.6) * mm, "radius": 5.75 * mm});
            skCircle(sketch, "E182.2.5.0", {"center": v(1625.6, 1270) * mm, "radius": 5.75 * mm});
            skCircle(sketch, "E182.2.6.0", {"center": v(1625.6, 1168.4) * mm, "radius": 5.75 * mm});
            skCircle(sketch, "E182.2.7.0", {"center": v(1625.6, 1066.8) * mm, "radius": 5.75 * mm});
            skCircle(sketch, "E182.2.8.0", {"center": v(1625.6, 965.2) * mm, "radius": 5.75 * mm});
            skCircle(sketch, "E182.2.9.0", {"center": v(1625.6, 863.6) * mm, "radius": 5.75 * mm});
            skCircle(sketch, "E182.2.10.0", {"center": v(1625.6, 762) * mm, "radius": 5.75 * mm});
            skCircle(sketch, "E182.2.11.0", {"center": v(1625.6, 660.4) * mm, "radius": 5.75 * mm});
            skCircle(sketch, "E182.2.12.0", {"center": v(1625.6, 558.8) * mm, "radius": 5.75 * mm});
            skCircle(sketch, "E182.2.13.0", {"center": v(1625.6, 457.2) * mm, "radius": 5.75 * mm});
            skCircle(sketch, "E182.2.14.0", {"center": v(1625.6, 355.6) * mm, "radius": 5.75 * mm});
            skCircle(sketch, "E182.2.15.0", {"center": v(1625.6, 254) * mm, "radius": 5.75 * mm});
            skCircle(sketch, "E182.2.16.0", {"center": v(1625.6, 152.4) * mm, "radius": 5.75 * mm});
            skCircle(sketch, "E182.2.17.0", {"center": v(1625.6, 50.8) * mm, "radius": 5.75 * mm});
            skCircle(sketch, "E182.3.0.0", {"center": v(1727.2, 1778) * mm, "radius": 5.75 * mm});
            skCircle(sketch, "E182.3.1.0", {"center": v(1727.2, 1676.4) * mm, "radius": 5.75 * mm});
            skCircle(sketch, "E182.3.2.0", {"center": v(1727.2, 1574.8) * mm, "radius": 5.75 * mm});
            skCircle(sketch, "E182.3.3.0", {"center": v(1727.2, 1473.2) * mm, "radius": 5.75 * mm});
            skCircle(sketch, "E182.3.4.0", {"center": v(1727.2, 1371.6) * mm, "radius": 5.75 * mm});
            skCircle(sketch, "E182.3.5.0", {"center": v(1727.2, 1270) * mm, "radius": 5.75 * mm});
            skCircle(sketch, "E182.3.6.0", {"center": v(1727.2, 1168.4) * mm, "radius": 5.75 * mm});
            skCircle(sketch, "E182.3.7.0", {"center": v(1727.2, 1066.8) * mm, "radius": 5.75 * mm});
            skCircle(sketch, "E182.3.8.0", {"center": v(1727.2, 965.2) * mm, "radius": 5.75 * mm});
            skCircle(sketch, "E182.3.9.0", {"center": v(1727.2, 863.6) * mm, "radius": 5.75 * mm});
            skCircle(sketch, "E182.3.10.0", {"center": v(1727.2, 762) * mm, "radius": 5.75 * mm});
            skCircle(sketch, "E182.3.11.0", {"center": v(1727.2, 660.4) * mm, "radius": 5.75 * mm});
            skCircle(sketch, "E182.3.12.0", {"center": v(1727.2, 558.8) * mm, "radius": 5.75 * mm});
            skCircle(sketch, "E182.3.13.0", {"center": v(1727.2, 457.2) * mm, "radius": 5.75 * mm});
            skCircle(sketch, "E182.3.14.0", {"center": v(1727.2, 355.6) * mm, "radius": 5.75 * mm});
            skCircle(sketch, "E182.3.15.0", {"center": v(1727.2, 254) * mm, "radius": 5.75 * mm});
            skCircle(sketch, "E182.3.16.0", {"center": v(1727.2, 152.4) * mm, "radius": 5.75 * mm});
            skCircle(sketch, "E182.3.17.0", {"center": v(1727.2, 50.8) * mm, "radius": 5.75 * mm});
            skCircle(sketch, "E182.4.0.0", {"center": v(1828.8, 1778) * mm, "radius": 5.75 * mm});
            skCircle(sketch, "E182.4.1.0", {"center": v(1828.8, 1676.4) * mm, "radius": 5.75 * mm});
            skCircle(sketch, "E182.4.2.0", {"center": v(1828.8, 1574.8) * mm, "radius": 5.75 * mm});
            skCircle(sketch, "E182.4.3.0", {"center": v(1828.8, 1473.2) * mm, "radius": 5.75 * mm});
            skCircle(sketch, "E182.4.4.0", {"center": v(1828.8, 1371.6) * mm, "radius": 5.75 * mm});
            skCircle(sketch, "E182.4.5.0", {"center": v(1828.8, 1270) * mm, "radius": 5.75 * mm});
            skCircle(sketch, "E182.4.6.0", {"center": v(1828.8, 1168.4) * mm, "radius": 5.75 * mm});
            skCircle(sketch, "E182.4.7.0", {"center": v(1828.8, 1066.8) * mm, "radius": 5.75 * mm});
            skCircle(sketch, "E182.4.8.0", {"center": v(1828.8, 965.2) * mm, "radius": 5.75 * mm});
            skCircle(sketch, "E182.4.9.0", {"center": v(1828.8, 863.6) * mm, "radius": 5.75 * mm});
            skCircle(sketch, "E182.4.10.0", {"center": v(1828.8, 762) * mm, "radius": 5.75 * mm});
            skCircle(sketch, "E182.4.11.0", {"center": v(1828.8, 660.4) * mm, "radius": 5.75 * mm});
            skCircle(sketch, "E182.4.12.0", {"center": v(1828.8, 558.8) * mm, "radius": 5.75 * mm});
            skCircle(sketch, "E182.4.13.0", {"center": v(1828.8, 457.2) * mm, "radius": 5.75 * mm});
            skCircle(sketch, "E182.4.14.0", {"center": v(1828.8, 355.6) * mm, "radius": 5.75 * mm});
            skCircle(sketch, "E182.4.15.0", {"center": v(1828.8, 254) * mm, "radius": 5.75 * mm});
            skCircle(sketch, "E182.4.16.0", {"center": v(1828.8, 152.4) * mm, "radius": 5.75 * mm});
            skCircle(sketch, "E182.4.17.0", {"center": v(1828.8, 50.8) * mm, "radius": 5.75 * mm});
            skCircle(sketch, "E182.5.0.0", {"center": v(1930.4, 1778) * mm, "radius": 5.75 * mm});
            skCircle(sketch, "E182.5.1.0", {"center": v(1930.4, 1676.4) * mm, "radius": 5.75 * mm});
            skCircle(sketch, "E182.5.2.0", {"center": v(1930.4, 1574.8) * mm, "radius": 5.75 * mm});
            skCircle(sketch, "E182.5.3.0", {"center": v(1930.4, 1473.2) * mm, "radius": 5.75 * mm});
            skCircle(sketch, "E182.5.4.0", {"center": v(1930.4, 1371.6) * mm, "radius": 5.75 * mm});
            skCircle(sketch, "E182.5.5.0", {"center": v(1930.4, 1270) * mm, "radius": 5.75 * mm});
            skCircle(sketch, "E182.5.6.0", {"center": v(1930.4, 1168.4) * mm, "radius": 5.75 * mm});
            skCircle(sketch, "E182.5.7.0", {"center": v(1930.4, 1066.8) * mm, "radius": 5.75 * mm});
            skCircle(sketch, "E182.5.8.0", {"center": v(1930.4, 965.2) * mm, "radius": 5.75 * mm});
            skCircle(sketch, "E182.5.9.0", {"center": v(1930.4, 863.6) * mm, "radius": 5.75 * mm});
            skCircle(sketch, "E182.5.10.0", {"center": v(1930.4, 762) * mm, "radius": 5.75 * mm});
            skCircle(sketch, "E182.5.11.0", {"center": v(1930.4, 660.4) * mm, "radius": 5.75 * mm});
            skCircle(sketch, "E182.5.12.0", {"center": v(1930.4, 558.8) * mm, "radius": 5.75 * mm});
            skCircle(sketch, "E182.5.13.0", {"center": v(1930.4, 457.2) * mm, "radius": 5.75 * mm});
            skCircle(sketch, "E182.5.14.0", {"center": v(1930.4, 355.6) * mm, "radius": 5.75 * mm});
            skCircle(sketch, "E182.5.15.0", {"center": v(1930.4, 254) * mm, "radius": 5.75 * mm});
            skCircle(sketch, "E182.5.16.0", {"center": v(1930.4, 152.4) * mm, "radius": 5.75 * mm});
            skCircle(sketch, "E182.5.17.0", {"center": v(1930.4, 50.8) * mm, "radius": 5.75 * mm});
            skCircle(sketch, "E182.6.0.0", {"center": v(2032, 1778) * mm, "radius": 5.75 * mm});
            skCircle(sketch, "E182.6.1.0", {"center": v(2032, 1676.4) * mm, "radius": 5.75 * mm});
            skCircle(sketch, "E182.6.2.0", {"center": v(2032, 1574.8) * mm, "radius": 5.75 * mm});
            skCircle(sketch, "E182.6.3.0", {"center": v(2032, 1473.2) * mm, "radius": 5.75 * mm});
            skCircle(sketch, "E182.6.4.0", {"center": v(2032, 1371.6) * mm, "radius": 5.75 * mm});
            skCircle(sketch, "E182.6.5.0", {"center": v(2032, 1270) * mm, "radius": 5.75 * mm});
            skCircle(sketch, "E182.6.6.0", {"center": v(2032, 1168.4) * mm, "radius": 5.75 * mm});
            skCircle(sketch, "E182.6.7.0", {"center": v(2032, 1066.8) * mm, "radius": 5.75 * mm});
            skCircle(sketch, "E182.6.8.0", {"center": v(2032, 965.2) * mm, "radius": 5.75 * mm});
            skCircle(sketch, "E182.6.9.0", {"center": v(2032, 863.6) * mm, "radius": 5.75 * mm});
            skCircle(sketch, "E182.6.10.0", {"center": v(2032, 762) * mm, "radius": 5.75 * mm});
            skCircle(sketch, "E182.6.11.0", {"center": v(2032, 660.4) * mm, "radius": 5.75 * mm});
            skCircle(sketch, "E182.6.12.0", {"center": v(2032, 558.8) * mm, "radius": 5.75 * mm});
            skCircle(sketch, "E182.6.13.0", {"center": v(2032, 457.2) * mm, "radius": 5.75 * mm});
            skCircle(sketch, "E182.6.14.0", {"center": v(2032, 355.6) * mm, "radius": 5.75 * mm});
            skCircle(sketch, "E182.6.15.0", {"center": v(2032, 254) * mm, "radius": 5.75 * mm});
            skCircle(sketch, "E182.6.16.0", {"center": v(2032, 152.4) * mm, "radius": 5.75 * mm});
            skCircle(sketch, "E182.6.17.0", {"center": v(2032, 50.8) * mm, "radius": 5.75 * mm});
            skCircle(sketch, "E182.7.0.0", {"center": v(2133.6, 1778) * mm, "radius": 5.75 * mm});
            skCircle(sketch, "E182.7.1.0", {"center": v(2133.6, 1676.4) * mm, "radius": 5.75 * mm});
            skCircle(sketch, "E182.7.2.0", {"center": v(2133.6, 1574.8) * mm, "radius": 5.75 * mm});
            skCircle(sketch, "E182.7.3.0", {"center": v(2133.6, 1473.2) * mm, "radius": 5.75 * mm});
            skCircle(sketch, "E182.7.4.0", {"center": v(2133.6, 1371.6) * mm, "radius": 5.75 * mm});
            skCircle(sketch, "E182.7.5.0", {"center": v(2133.6, 1270) * mm, "radius": 5.75 * mm});
            skCircle(sketch, "E182.7.6.0", {"center": v(2133.6, 1168.4) * mm, "radius": 5.75 * mm});
            skCircle(sketch, "E182.7.7.0", {"center": v(2133.6, 1066.8) * mm, "radius": 5.75 * mm});
            skCircle(sketch, "E182.7.8.0", {"center": v(2133.6, 965.2) * mm, "radius": 5.75 * mm});
            skCircle(sketch, "E182.7.9.0", {"center": v(2133.6, 863.6) * mm, "radius": 5.75 * mm});
            skCircle(sketch, "E182.7.10.0", {"center": v(2133.6, 762) * mm, "radius": 5.75 * mm});
            skCircle(sketch, "E182.7.11.0", {"center": v(2133.6, 660.4) * mm, "radius": 5.75 * mm});
            skCircle(sketch, "E182.7.12.0", {"center": v(2133.6, 558.8) * mm, "radius": 5.75 * mm});
            skCircle(sketch, "E182.7.13.0", {"center": v(2133.6, 457.2) * mm, "radius": 5.75 * mm});
            skCircle(sketch, "E182.7.14.0", {"center": v(2133.6, 355.6) * mm, "radius": 5.75 * mm});
            skCircle(sketch, "E182.7.15.0", {"center": v(2133.6, 254) * mm, "radius": 5.75 * mm});
            skCircle(sketch, "E182.7.16.0", {"center": v(2133.6, 152.4) * mm, "radius": 5.75 * mm});
            skCircle(sketch, "E182.7.17.0", {"center": v(2133.6, 50.8) * mm, "radius": 5.75 * mm});
            skCircle(sketch, "E182.8.0.0", {"center": v(2235.2, 1778) * mm, "radius": 5.75 * mm});
            skCircle(sketch, "E182.8.1.0", {"center": v(2235.2, 1676.4) * mm, "radius": 5.75 * mm});
            skCircle(sketch, "E182.8.2.0", {"center": v(2235.2, 1574.8) * mm, "radius": 5.75 * mm});
            skCircle(sketch, "E182.8.3.0", {"center": v(2235.2, 1473.2) * mm, "radius": 5.75 * mm});
            skCircle(sketch, "E182.8.4.0", {"center": v(2235.2, 1371.6) * mm, "radius": 5.75 * mm});
            skCircle(sketch, "E182.8.5.0", {"center": v(2235.2, 1270) * mm, "radius": 5.75 * mm});
            skCircle(sketch, "E182.8.6.0", {"center": v(2235.2, 1168.4) * mm, "radius": 5.75 * mm});
            skCircle(sketch, "E182.8.7.0", {"center": v(2235.2, 1066.8) * mm, "radius": 5.75 * mm});
            skCircle(sketch, "E182.8.8.0", {"center": v(2235.2, 965.2) * mm, "radius": 5.75 * mm});
            skCircle(sketch, "E182.8.9.0", {"center": v(2235.2, 863.6) * mm, "radius": 5.75 * mm});
            skCircle(sketch, "E182.8.10.0", {"center": v(2235.2, 762) * mm, "radius": 5.75 * mm});
            skCircle(sketch, "E182.8.11.0", {"center": v(2235.2, 660.4) * mm, "radius": 5.75 * mm});
            skCircle(sketch, "E182.8.12.0", {"center": v(2235.2, 558.8) * mm, "radius": 5.75 * mm});
            skCircle(sketch, "E182.8.13.0", {"center": v(2235.2, 457.2) * mm, "radius": 5.75 * mm});
            skCircle(sketch, "E182.8.14.0", {"center": v(2235.2, 355.6) * mm, "radius": 5.75 * mm});
            skCircle(sketch, "E182.8.15.0", {"center": v(2235.2, 254) * mm, "radius": 5.75 * mm});
            skCircle(sketch, "E182.8.16.0", {"center": v(2235.2, 152.4) * mm, "radius": 5.75 * mm});
            skCircle(sketch, "E182.8.17.0", {"center": v(2235.2, 50.8) * mm, "radius": 5.75 * mm});
            skCircle(sketch, "E182.9.0.0", {"center": v(2336.8, 1778) * mm, "radius": 5.75 * mm});
            skCircle(sketch, "E182.9.1.0", {"center": v(2336.8, 1676.4) * mm, "radius": 5.75 * mm});
            skCircle(sketch, "E182.9.2.0", {"center": v(2336.8, 1574.8) * mm, "radius": 5.75 * mm});
            skCircle(sketch, "E182.9.3.0", {"center": v(2336.8, 1473.2) * mm, "radius": 5.75 * mm});
            skCircle(sketch, "E182.9.4.0", {"center": v(2336.8, 1371.6) * mm, "radius": 5.75 * mm});
            skCircle(sketch, "E182.9.5.0", {"center": v(2336.8, 1270) * mm, "radius": 5.75 * mm});
            skCircle(sketch, "E182.9.6.0", {"center": v(2336.8, 1168.4) * mm, "radius": 5.75 * mm});
            skCircle(sketch, "E182.9.7.0", {"center": v(2336.8, 1066.8) * mm, "radius": 5.75 * mm});
            skCircle(sketch, "E182.9.8.0", {"center": v(2336.8, 965.2) * mm, "radius": 5.75 * mm});
            skCircle(sketch, "E182.9.9.0", {"center": v(2336.8, 863.6) * mm, "radius": 5.75 * mm});
            skCircle(sketch, "E182.9.10.0", {"center": v(2336.8, 762) * mm, "radius": 5.75 * mm});
            skCircle(sketch, "E182.9.11.0", {"center": v(2336.8, 660.4) * mm, "radius": 5.75 * mm});
            skCircle(sketch, "E182.9.12.0", {"center": v(2336.8, 558.8) * mm, "radius": 5.75 * mm});
            skCircle(sketch, "E182.9.13.0", {"center": v(2336.8, 457.2) * mm, "radius": 5.75 * mm});
            skCircle(sketch, "E182.9.14.0", {"center": v(2336.8, 355.6) * mm, "radius": 5.75 * mm});
            skCircle(sketch, "E182.9.15.0", {"center": v(2336.8, 254) * mm, "radius": 5.75 * mm});
            skCircle(sketch, "E182.9.16.0", {"center": v(2336.8, 152.4) * mm, "radius": 5.75 * mm});
            skCircle(sketch, "E182.9.17.0", {"center": v(2336.8, 50.8) * mm, "radius": 5.75 * mm});
            skCircle(sketch, "E182.10.0.0", {"center": v(2438.4, 1778) * mm, "radius": 5.75 * mm});
            skCircle(sketch, "E182.10.1.0", {"center": v(2438.4, 1676.4) * mm, "radius": 5.75 * mm});
            skCircle(sketch, "E182.10.2.0", {"center": v(2438.4, 1574.8) * mm, "radius": 5.75 * mm});
            skCircle(sketch, "E182.10.3.0", {"center": v(2438.4, 1473.2) * mm, "radius": 5.75 * mm});
            skCircle(sketch, "E182.10.4.0", {"center": v(2438.4, 1371.6) * mm, "radius": 5.75 * mm});
            skCircle(sketch, "E182.10.5.0", {"center": v(2438.4, 1270) * mm, "radius": 5.75 * mm});
            skCircle(sketch, "E182.10.6.0", {"center": v(2438.4, 1168.4) * mm, "radius": 5.75 * mm});
            skCircle(sketch, "E182.10.7.0", {"center": v(2438.4, 1066.8) * mm, "radius": 5.75 * mm});
            skCircle(sketch, "E182.10.8.0", {"center": v(2438.4, 965.2) * mm, "radius": 5.75 * mm});
            skCircle(sketch, "E182.10.9.0", {"center": v(2438.4, 863.6) * mm, "radius": 5.75 * mm});
            skCircle(sketch, "E182.10.10.0", {"center": v(2438.4, 762) * mm, "radius": 5.75 * mm});
            skCircle(sketch, "E182.10.11.0", {"center": v(2438.4, 660.4) * mm, "radius": 5.75 * mm});
            skCircle(sketch, "E182.10.12.0", {"center": v(2438.4, 558.8) * mm, "radius": 5.75 * mm});
            skCircle(sketch, "E182.10.13.0", {"center": v(2438.4, 457.2) * mm, "radius": 5.75 * mm});
            skCircle(sketch, "E182.10.14.0", {"center": v(2438.4, 355.6) * mm, "radius": 5.75 * mm});
            skCircle(sketch, "E182.10.15.0", {"center": v(2438.4, 254) * mm, "radius": 5.75 * mm});
            skCircle(sketch, "E182.10.16.0", {"center": v(2438.4, 152.4) * mm, "radius": 5.75 * mm});
            skCircle(sketch, "E182.10.17.0", {"center": v(2438.4, 50.8) * mm, "radius": 5.75 * mm});
            skCircle(sketch, "E182.11.0.0", {"center": v(2540, 1778) * mm, "radius": 5.75 * mm});
            skCircle(sketch, "E182.11.1.0", {"center": v(2540, 1676.4) * mm, "radius": 5.75 * mm});
            skCircle(sketch, "E182.11.2.0", {"center": v(2540, 1574.8) * mm, "radius": 5.75 * mm});
            skCircle(sketch, "E182.11.3.0", {"center": v(2540, 1473.2) * mm, "radius": 5.75 * mm});
            skCircle(sketch, "E182.11.4.0", {"center": v(2540, 1371.6) * mm, "radius": 5.75 * mm});
            skCircle(sketch, "E182.11.5.0", {"center": v(2540, 1270) * mm, "radius": 5.75 * mm});
            skCircle(sketch, "E182.11.6.0", {"center": v(2540, 1168.4) * mm, "radius": 5.75 * mm});
            skCircle(sketch, "E182.11.7.0", {"center": v(2540, 1066.8) * mm, "radius": 5.75 * mm});
            skCircle(sketch, "E182.11.8.0", {"center": v(2540, 965.2) * mm, "radius": 5.75 * mm});
            skCircle(sketch, "E182.11.9.0", {"center": v(2540, 863.6) * mm, "radius": 5.75 * mm});
            skCircle(sketch, "E182.11.10.0", {"center": v(2540, 762) * mm, "radius": 5.75 * mm});
            skCircle(sketch, "E182.11.11.0", {"center": v(2540, 660.4) * mm, "radius": 5.75 * mm});
            skCircle(sketch, "E182.11.12.0", {"center": v(2540, 558.8) * mm, "radius": 5.75 * mm});
            skCircle(sketch, "E182.11.13.0", {"center": v(2540, 457.2) * mm, "radius": 5.75 * mm});
            skCircle(sketch, "E182.11.14.0", {"center": v(2540, 355.6) * mm, "radius": 5.75 * mm});
            skCircle(sketch, "E182.11.15.0", {"center": v(2540, 254) * mm, "radius": 5.75 * mm});
            skCircle(sketch, "E182.11.16.0", {"center": v(2540, 152.4) * mm, "radius": 5.75 * mm});
            skCircle(sketch, "E182.11.17.0", {"center": v(2540, 50.8) * mm, "radius": 5.75 * mm});
            skLineSegment(sketch, "E182.direction1", {"start": v(1422.4, 1778) * mm, "end": v(1524, 1778) * mm, "construction": true});
            skLineSegment(sketch, "E182.direction2", {"start": v(1422.4, 1778) * mm, "end": v(1422.4, 1676.4) * mm, "construction": true});
            skCircle(sketch, "E183", {"center": v(1422.4, 914.4) * mm, "radius": 2.41 * mm});
            skCircle(sketch, "E184", {"center": v(1981.2, 914.4) * mm, "radius": 2.41 * mm});
            skCircle(sketch, "E185", {"center": v(1828.8, 914.4) * mm, "radius": 2.41 * mm});
            skCircle(sketch, "E186", {"center": v(1676.4, 914.4) * mm, "radius": 2.41 * mm});
            skCircle(sketch, "E187", {"center": v(1524, 914.4) * mm, "radius": 2.41 * mm});
            skCircle(sketch, "E188.0.1.0", {"center": v(1981.2, 1219.2) * mm, "radius": 2.41 * mm});
            skCircle(sketch, "E188.1.1.0", {"center": v(1676.4, 1219.2) * mm, "radius": 2.41 * mm});
            skLineSegment(sketch, "E188.direction1", {"start": v(1981.2, 914.4) * mm, "end": v(1676.4, 914.4) * mm, "construction": true});
            skLineSegment(sketch, "E188.direction2", {"start": v(1981.2, 914.4) * mm, "end": v(1981.2, 1219.2) * mm, "construction": true});
            skCircle(sketch, "E189.0.0.2", {"center": v(1981.2, 1524) * mm, "radius": 2.41 * mm});
            skCircle(sketch, "E189.0.1.2", {"center": v(1676.4, 1524) * mm, "radius": 2.41 * mm});
            skCircle(sketch, "E190", {"center": v(1981.2, 1778) * mm, "radius": 2.41 * mm});
            skSolve(sketch);
        }
        {
            var Q0;
            Q0 = qSketchRegion(id + "F10", true);
            extrude(context, id + "F11", {"entities" : qUnion([Q0]), "operationType" : NewBodyOperationType.REMOVE, "oppositeDirection" : true, "depth" : 19.05 * mm, "offsetDistance" : 25.4 * mm});
        }
    });
